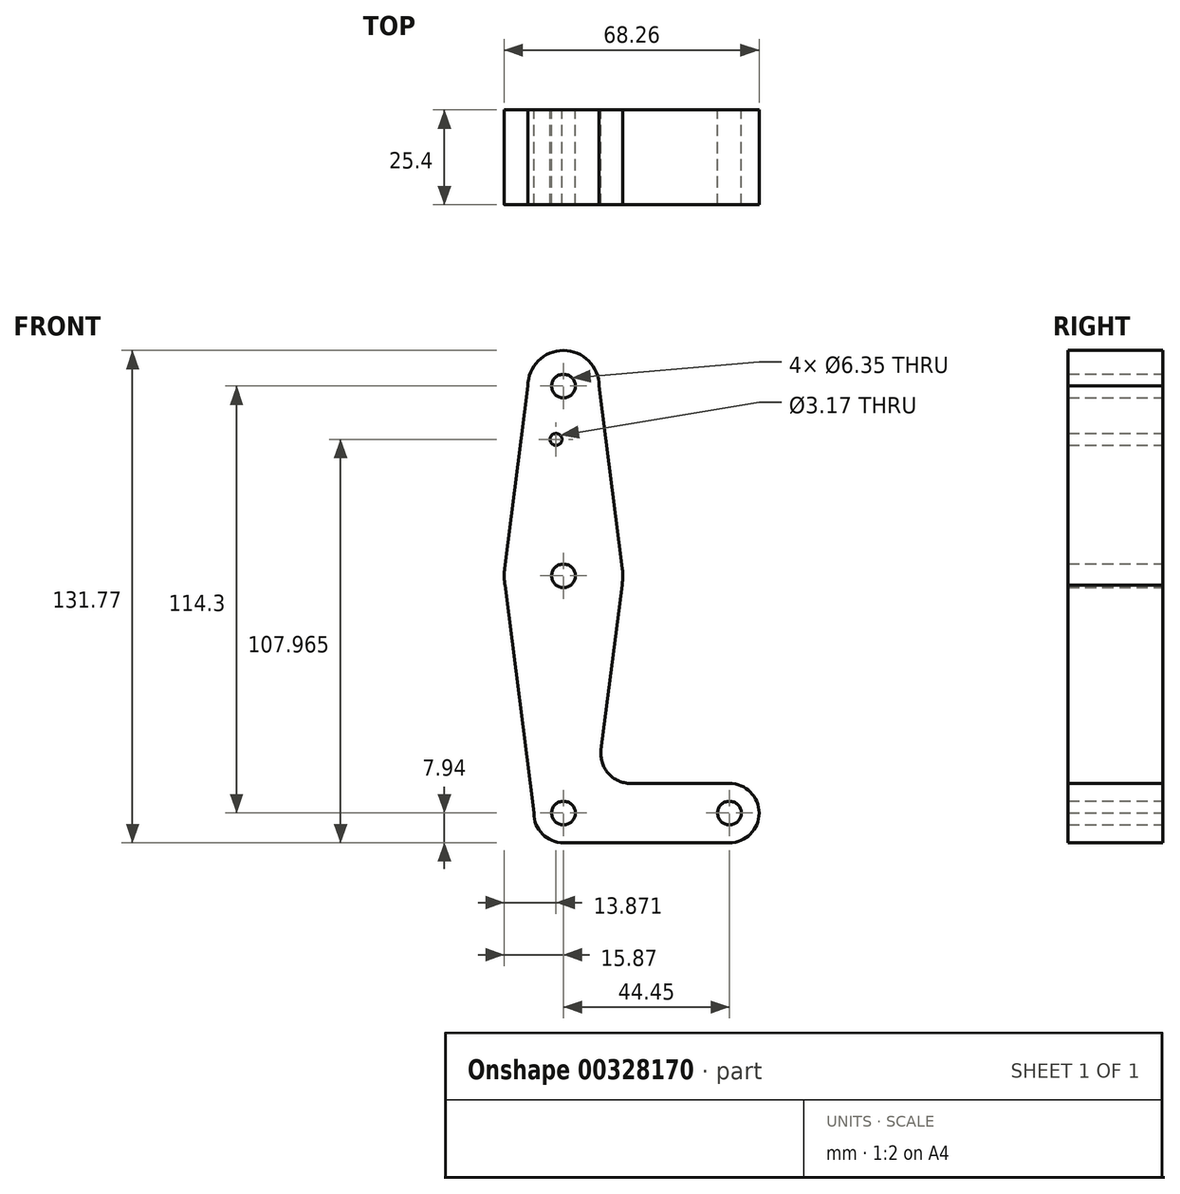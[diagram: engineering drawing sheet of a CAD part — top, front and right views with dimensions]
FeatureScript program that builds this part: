
annotation { "Feature Type Name" : "Feature", "Feature Type Description" : "" }
export const myFeature = defineFeature(function(context is Context, id is Id, definition is map)
    precondition{}
    {
        {
            var Q0;
            Q0=qCreatedBy(makeId("Front.planeOp"),FACE);
            var sketch = newSketch(context, id + "F0", { "sketchPlane" : qUnion([Q0])});
            skLineSegment(sketch, "E0", {"start": v(0, 114.3) * mm, "end": v(0, 0) * mm, "construction": true});
            skLineSegment(sketch, "E1", {"start": v(0, 0) * mm, "end": v(44.45, 0) * mm, "construction": true});
            skCircle(sketch, "E2", {"center": v(44.45, 0) * mm, "radius": 7.94 * mm});
            skCircle(sketch, "E3", {"center": v(0, 0) * mm, "radius": 7.94 * mm});
            skCircle(sketch, "E4", {"center": v(0, 63.5) * mm, "radius": 15.88 * mm});
            skCircle(sketch, "E5", {"center": v(0, 114.3) * mm, "radius": 9.53 * mm});
            skLineSegment(sketch, "E6", {"start": v(0, -7.94) * mm, "end": v(44.45, -7.94) * mm});
            skCircle(sketch, "E7", {"center": v(0, 63.5) * mm, "radius": 3.18 * mm});
            skCircle(sketch, "E8", {"center": v(0, 0) * mm, "radius": 3.18 * mm});
            skCircle(sketch, "E9", {"center": v(44.45, 0) * mm, "radius": 3.18 * mm});
            skCircle(sketch, "E10", {"center": v(0, 114.3) * mm, "radius": 3.18 * mm});
            skLineSegment(sketch, "E11", {"start": v(17.97, 7.94) * mm, "end": v(44.45, 7.94) * mm});
            skLineSegment(sketch, "E12", {"start": v(-9.53, 114.3) * mm, "end": v(-15.75, 65.5) * mm});
            skLineSegment(sketch, "E13", {"start": v(9.52, 114.3) * mm, "end": v(15.75, 65.5) * mm});
            skLineSegment(sketch, "E14", {"start": v(-15.8, 62) * mm, "end": v(-7.94, 0) * mm});
            skLineSegment(sketch, "E15", {"start": v(15.8, 62) * mm, "end": v(10.08, 16.89) * mm});
            skCircle(sketch, "E16", {"center": v(-2, 100.03) * mm, "radius": 1.59 * mm});
            skArc(sketch, "E17.filletArc", {"start": v(10.08, 16.89) * mm, "mid": v(12, 10.63) * mm, "end": v(17.97, 7.94) * mm});
            skSolve(sketch);
        }
        {
            var Q0;
            Q0 = qSketchRegion(id + "F0", true);
            var Q1;
            {var subQ0=sQuery(id+"F0.wireOp",EDGE,"E3");var subQ1=sQuery(id+"F0.wireOp",EDGE,"E0");var subQ2=makeQuery(id+"F0.imprint","INTERSECT",VERTEX,{"derivedFrom":[subQ1,subQ0]});Q1=makeQuery(id+"F0.imprint","IMPRINT",FACE,{"disambiguationData":[TD([[makeQuery(id+"F0.imprint","IMPRINT",EDGE,{"disambiguationData":[TD([[subQ2,-1.0]])],"derivedFrom":subQ1}),1.0]])]});}
            extrude(context, id + "F1", {"entities" : qUnion([Q0, Q1]), "depth" : 25.4 * mm});
        }
    });
